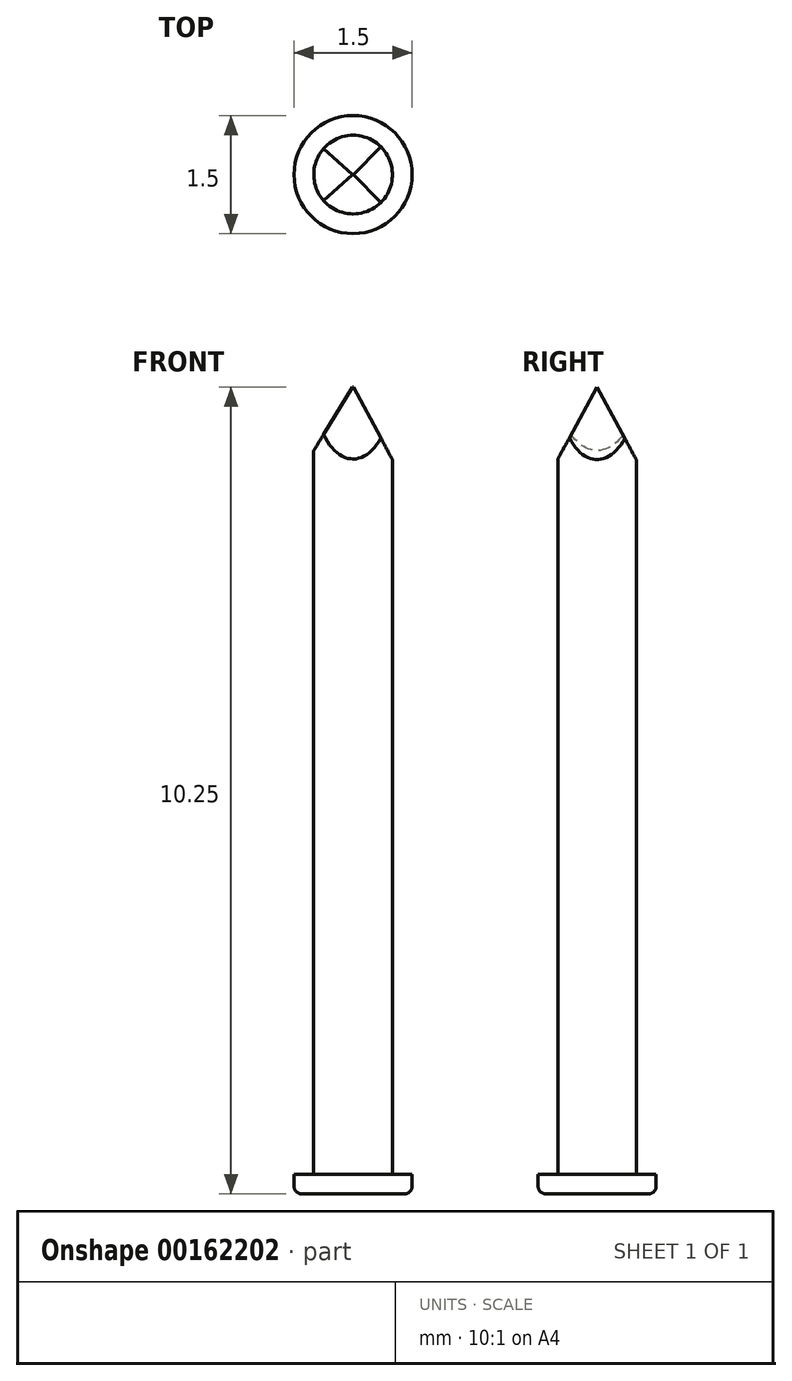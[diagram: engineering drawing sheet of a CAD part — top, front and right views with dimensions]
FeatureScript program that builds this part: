
annotation { "Feature Type Name" : "Feature", "Feature Type Description" : "" }
export const myFeature = defineFeature(function(context is Context, id is Id, definition is map)
    precondition{}
    {
        {
            var Q0;
            Q0=qCreatedBy(makeId("Top.planeOp"),FACE);
            var sketch = newSketch(context, id + "F0", { "sketchPlane" : qUnion([Q0])});
            skCircle(sketch, "E0", {"center": v(0, 0) * mm, "radius": 0.5 * mm});
            skCircle(sketch, "E1", {"center": v(0, 0) * mm, "radius": 0.75 * mm});
            skSolve(sketch);
        }
        {
            var Q0;
            Q0=makeQuery(id+"F0.imprint","IMPRINT",FACE,{"disambiguationData":[TD([[makeQuery(id+"F0.imprint","IMPRINT",EDGE,{"derivedFrom":sQuery(id+"F0.wireOp",EDGE,"E0")}),1.0]])]});
            extrude(context, id + "F1", {"entities" : qUnion([Q0]), "depth" : 10 * mm});
        }
        {
            var Q0;
            Q0=makeQuery(id+"F0.imprint","IMPRINT",FACE,{"disambiguationData":[TD([[makeQuery(id+"F0.imprint","IMPRINT",EDGE,{"derivedFrom":sQuery(id+"F0.wireOp",EDGE,"E0")}),-1.0]])]});
            var Q1;
            Q1=makeQuery(id+"F0.imprint","IMPRINT",FACE,{"disambiguationData":[TD([[makeQuery(id+"F0.imprint","IMPRINT",EDGE,{"derivedFrom":sQuery(id+"F0.wireOp",EDGE,"E0")}),1.0]])]});
            extrude(context, id + "F2", {"entities" : qUnion([Q0, Q1]), "operationType" : NewBodyOperationType.ADD, "oppositeDirection" : true, "depth" : .25 * mm});
        }
        {
            var Q0;
            Q0=makeQuery(id+"F2.opExtrude","CAP_EDGE",EDGE,{"disambiguationData":[OSD([sQuery(id+"F0.wireOp",EDGE,"E1")])],"isStart":false});
            fillet(context, id + "F3", {"entities" : qUnion([Q0]), "radius" : .1 * mm, "tangentPropagation" : true, "allowEdgeOverflow" : false});
        }
        {
            var Q0;
            Q0=qCreatedBy(makeId("Right.planeOp"),FACE);
            var sketch = newSketch(context, id + "F4", { "sketchPlane" : qUnion([Q0])});
            skLineSegment(sketch, "E2", {"start": v(0, 10) * mm, "end": v(-0.68, 8.76) * mm});
            skLineSegment(sketch, "E3", {"start": v(-0.68, 8.76) * mm, "end": v(-0.8, 10.7) * mm});
            skLineSegment(sketch, "E4", {"start": v(-0.8, 10.7) * mm, "end": v(0.7, 10.7) * mm});
            skLineSegment(sketch, "E5", {"start": v(0.7, 10.7) * mm, "end": v(0.7, 8.72) * mm});
            skLineSegment(sketch, "E6", {"start": v(0.7, 8.72) * mm, "end": v(0, 10) * mm});
            skSolve(sketch);
        }
        {
            var Q0;
            Q0=makeQuery(id+"F4.imprint","IMPRINT",FACE,{"disambiguationData":[TD([[makeQuery(id+"F4.imprint","IMPRINT",EDGE,{"derivedFrom":sQuery(id+"F4.wireOp",EDGE,"E2")}),-1.0]])]});
            extrude(context, id + "F5", {"entities" : qUnion([Q0]), "operationType" : NewBodyOperationType.REMOVE, "depth" : 25 * mm, "hasSecondDirection" : true, "secondDirectionOppositeDirection" : true, "secondDirectionDepth" : 25 * mm});
        }
        {
            var Q0;
            Q0=qCreatedBy(makeId("Front.planeOp"),FACE);
            var sketch = newSketch(context, id + "F6", { "sketchPlane" : qUnion([Q0])});
            skLineSegment(sketch, "E7", {"start": v(0, 10) * mm, "end": v(0.68, 8.75) * mm});
            skLineSegment(sketch, "E8", {"start": v(0.68, 8.75) * mm, "end": v(0.68, 10.3) * mm});
            skLineSegment(sketch, "E9", {"start": v(0.68, 10.3) * mm, "end": v(-0.8, 10.3) * mm});
            skLineSegment(sketch, "E10", {"start": v(-0.8, 10.3) * mm, "end": v(-0.8, 8.72) * mm});
            skLineSegment(sketch, "E11", {"start": v(-0.8, 8.72) * mm, "end": v(0, 10) * mm});
            skSolve(sketch);
        }
        {
            var Q0;
            Q0=makeQuery(id+"F6.imprint","IMPRINT",FACE,{"disambiguationData":[TD([[makeQuery(id+"F6.imprint","IMPRINT",EDGE,{"derivedFrom":sQuery(id+"F6.wireOp",EDGE,"E7")}),1.0]])]});
            extrude(context, id + "F7", {"entities" : qUnion([Q0]), "operationType" : NewBodyOperationType.REMOVE, "depth" : 25 * mm, "hasSecondDirection" : true, "secondDirectionOppositeDirection" : true, "secondDirectionDepth" : 25 * mm});
        }
    });
